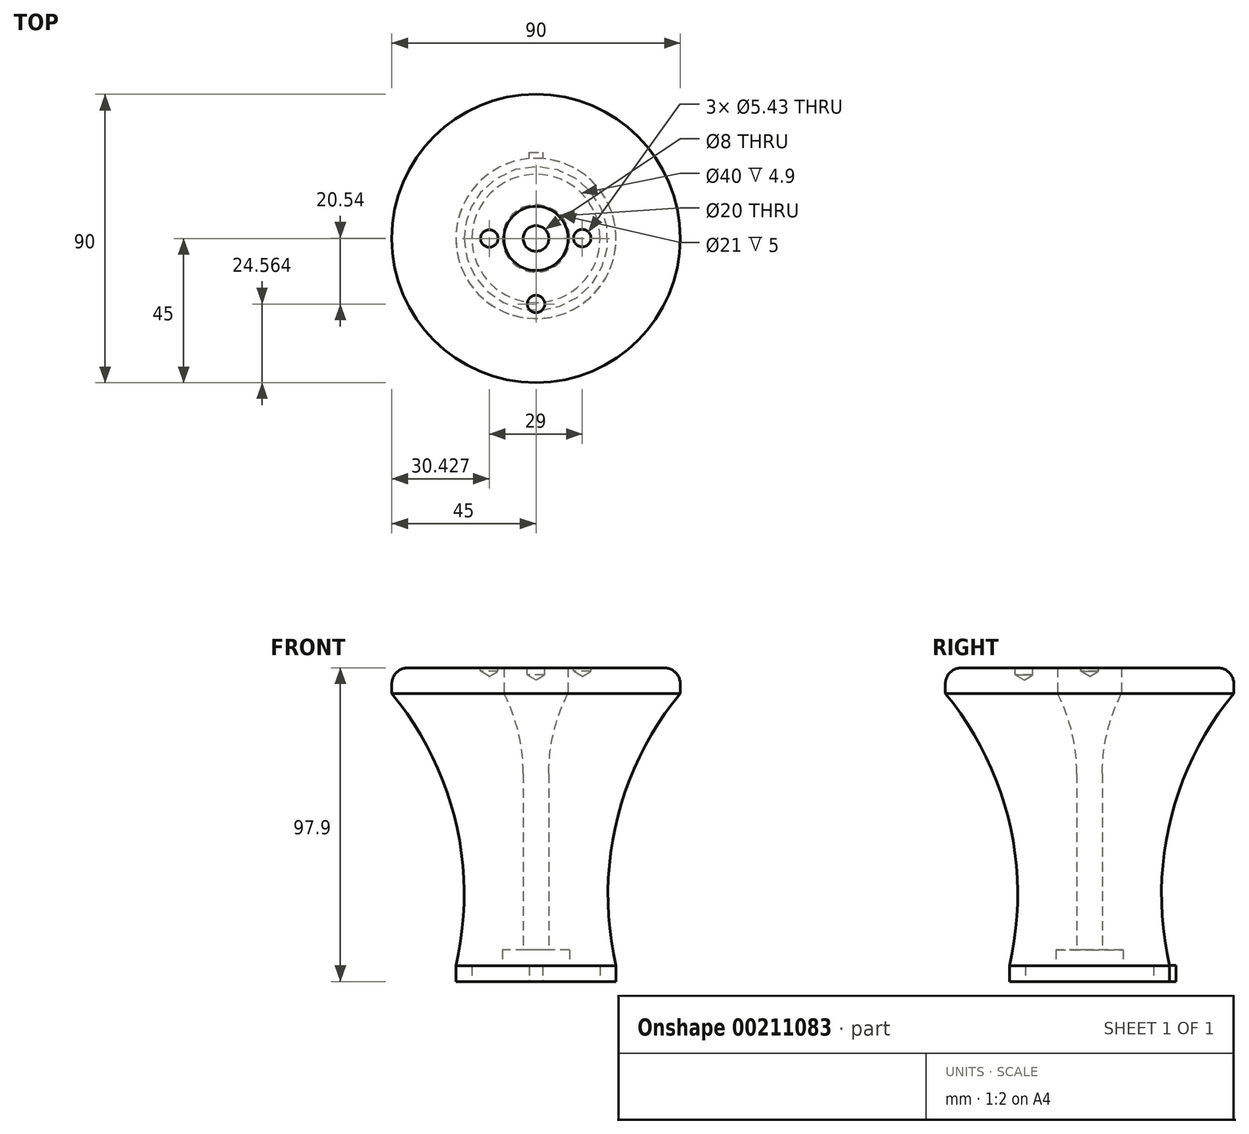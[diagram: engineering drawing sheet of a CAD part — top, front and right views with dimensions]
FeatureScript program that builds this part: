
annotation { "Feature Type Name" : "Feature", "Feature Type Description" : "" }
export const myFeature = defineFeature(function(context is Context, id is Id, definition is map)
    precondition{}
    {
        {
            var Q0;
            Q0=qCreatedBy(makeId("Front.planeOp"),FACE);
            var sketch = newSketch(context, id + "F0", { "sketchPlane" : qUnion([Q0])});
            skLineSegment(sketch, "E0", {"start": v(25, 0) * mm, "end": v(4, 0) * mm});
            skLineSegment(sketch, "E1", {"start": v(4, 0) * mm, "end": v(4, 60) * mm});
            skLineSegment(sketch, "E2", {"start": v(10, 85) * mm, "end": v(45, 85) * mm});
            skArc(sketch, "E3", {"start": v(45, 85) * mm, "mid": v(25.06, 44.84) * mm, "end": v(25, 0) * mm});
            skArc(sketch, "E4", {"start": v(10, 85) * mm, "mid": v(5.52, 72.85) * mm, "end": v(4, 60) * mm});
            skSolve(sketch);
        }
        {
            var Q0;
            Q0=qCreatedBy(makeId("Front.planeOp"),FACE);
            var sketch = newSketch(context, id + "F1", { "sketchPlane" : qUnion([Q0])});
            skLineSegment(sketch, "E5", {"start": v(0, 0) * mm, "end": v(0, 50.34) * mm});
            skSolve(sketch);
        }
        {
            var Q0;
            Q0=makeQuery(id+"F0.imprint","IMPRINT",FACE,{"disambiguationData":[TD([[makeQuery(id+"F0.imprint","IMPRINT",EDGE,{"derivedFrom":sQuery(id+"F0.wireOp",EDGE,"E0")}),-1.0]])]});
            var Q1;
            Q1=sQuery(id+"F1.wireOp",EDGE,"E5");
            revolve(context, id + "F2", {"entities" : qUnion([Q0]), "axis" : qUnion([Q1]), "revolveType" : RevolveType.FULL});
        }
        {
            var Q0;
            Q0=makeQuery(id+"F2.opRevolve","SWEPT_FACE",FACE,{"disambiguationData":[OSD([sQuery(id+"F0.wireOp",EDGE,"E0")])]});
            extrude(context, id + "F3", {"entities" : qUnion([Q0]), "operationType" : NewBodyOperationType.ADD, "depth" : 4.9 * mm});
        }
        {
            var Q0;
            Q0=makeQuery(id+"F3.opExtrude","CAP_FACE",FACE,{"disambiguationData":[OSD([sQuery(id+"F0.wireOp",EDGE,"E0")])],"isStart":false});
            var sketch = newSketch(context, id + "F4", { "sketchPlane" : qUnion([Q0])});
            skCircle(sketch, "E6", {"center": v(0, 0) * mm, "radius": 20 * mm});
            skSolve(sketch);
        }
        {
            var Q0;
            Q0=makeQuery(id+"F4.imprint","IMPRINT",FACE,{"disambiguationData":[TD([[makeQuery(id+"F4.imprint","IMPRINT",EDGE,{"derivedFrom":sQuery(id+"F4.wireOp",EDGE,"E6")}),1.0]])]});
            var Q1;
            Q1=sQuery(id+"F4.wireOp",EDGE,"E6");
            extrude(context, id + "F5", {"entities" : qUnion([Q0]), "operationType" : NewBodyOperationType.REMOVE, "surfaceEntities" : qUnion([Q1]), "oppositeDirection" : true, "depth" : 4.9 * mm});
        }
        {
            var Q0;
            Q0=makeQuery(id+"F2.opRevolve","SWEPT_FACE",FACE,{"disambiguationData":[OSD([sQuery(id+"F0.wireOp",EDGE,"E2")])]});
            extrude(context, id + "F6", {"entities" : qUnion([Q0]), "operationType" : NewBodyOperationType.ADD, "depth" : 8 * mm});
        }
        {
            var Q0;
            Q0=makeQuery(id+"F6.opExtrude","CAP_EDGE",EDGE,{"disambiguationData":[OSD([sQuery(id+"F0.wireOp",EDGE,"E2"),sQuery(id+"F0.wireOp",EDGE,"E3")])],"isStart":false});
            fillet(context, id + "F7", {"entities" : qUnion([Q0]), "radius" : 5 * mm, "tangentPropagation" : true, "allowEdgeOverflow" : false});
        }
        {
            var Q0;
            Q0=makeQuery(id+"F6.opExtrude","CAP_FACE",FACE,{"disambiguationData":[OSD([sQuery(id+"F0.wireOp",EDGE,"E2")])],"isStart":false});
            var sketch = newSketch(context, id + "F8", { "sketchPlane" : qUnion([Q0])});
            skPoint(sketch, "E7", {"position": v(0, -20.44) * mm});
            skPoint(sketch, "E8", {"position": v(-14.57, 0) * mm});
            skPoint(sketch, "E9", {"position": v(14.43, 0.1) * mm});
            skSolve(sketch);
        }
        {
            var Q0;
            Q0=sQuery(id+"F8.wireOp",VERTEX,"E9");
            var Q1;
            Q1=sQuery(id+"F8.wireOp",VERTEX,"E8");
            var Q2;
            Q2=makeQuery(id+"F2.opRevolve","SWEPT_BODY",BODY,{"disambiguationData":[OSD([sQuery(id+"F0.wireOp",EDGE,"E0"),sQuery(id+"F0.wireOp",EDGE,"E1"),sQuery(id+"F0.wireOp",EDGE,"E2"),sQuery(id+"F0.wireOp",EDGE,"E3"),sQuery(id+"F0.wireOp",EDGE,"E4")])]});
            hole(context, id + "F9", {"style" : HoleStyle.SIMPLE, "endStyle" : HoleEndStyle.BLIND, "holeDiameter" : 5.43 * mm, "holeDepth" : 1.1 * mm, "startFromSketch" : true, "locations" : qUnion([Q0, Q1]), "scope" : qUnion([Q2])});
        }
        {
            var Q0;
            Q0=sQuery(id+"F8.wireOp",VERTEX,"E7");
            var Q1;
            Q1=makeQuery(id+"F2.opRevolve","SWEPT_BODY",BODY,{"disambiguationData":[OSD([sQuery(id+"F0.wireOp",EDGE,"E0"),sQuery(id+"F0.wireOp",EDGE,"E1"),sQuery(id+"F0.wireOp",EDGE,"E2"),sQuery(id+"F0.wireOp",EDGE,"E3"),sQuery(id+"F0.wireOp",EDGE,"E4")])]});
            hole(context, id + "F10", {"style" : HoleStyle.SIMPLE, "endStyle" : HoleEndStyle.BLIND, "holeDiameter" : 5.43 * mm, "holeDepth" : 2.2 * mm, "startFromSketch" : true, "locations" : qUnion([Q0]), "scope" : qUnion([Q1])});
        }
        {
            var Q0;
            Q0=qCreatedBy(makeId("Top.planeOp"),FACE);
            var sketch = newSketch(context, id + "F11", { "sketchPlane" : qUnion([Q0])});
            skCircle(sketch, "E10", {"center": v(0, 0) * mm, "radius": 10.5 * mm});
            skSolve(sketch);
        }
        {
            var Q0;
            Q0 = qSketchRegion(id + "F11", true);
            extrude(context, id + "F12", {"entities" : qUnion([Q0]), "operationType" : NewBodyOperationType.REMOVE, "depth" : 5 * mm});
        }
        {
            var Q0;
            Q0=makeQuery(id+"F4.imprint","IMPRINT",FACE,{"disambiguationData":[TD([[makeQuery(id+"F4.imprint","IMPRINT",EDGE,{"derivedFrom":sQuery(id+"F4.wireOp",EDGE,"E6")}),-1.0]])]});
            var sketch = newSketch(context, id + "F13", { "sketchPlane" : qUnion([Q0])});
            skArc(sketch, "E11", {"start": v(-2.12, -24.9) * mm, "mid": v(0, -25) * mm, "end": v(2.13, -24.9) * mm});
            skLineSegment(sketch, "E12", {"start": v(0, 0) * mm, "end": v(0, -36.79) * mm, "construction": true});
            skLineSegment(sketch, "E13", {"start": v(-2.12, -24.9) * mm, "end": v(-2.12, -26.9) * mm});
            skLineSegment(sketch, "E14", {"start": v(-2.12, -26.9) * mm, "end": v(2.13, -26.9) * mm});
            skLineSegment(sketch, "E15", {"start": v(2.13, -26.9) * mm, "end": v(2.13, -24.9) * mm});
            skSolve(sketch);
        }
        {
            var Q0;
            Q0 = qSketchRegion(id + "F13", true);
            extrude(context, id + "F14", {"entities" : qUnion([Q0]), "operationType" : NewBodyOperationType.ADD, "oppositeDirection" : true, "depth" : 5 * mm});
        }
    });
